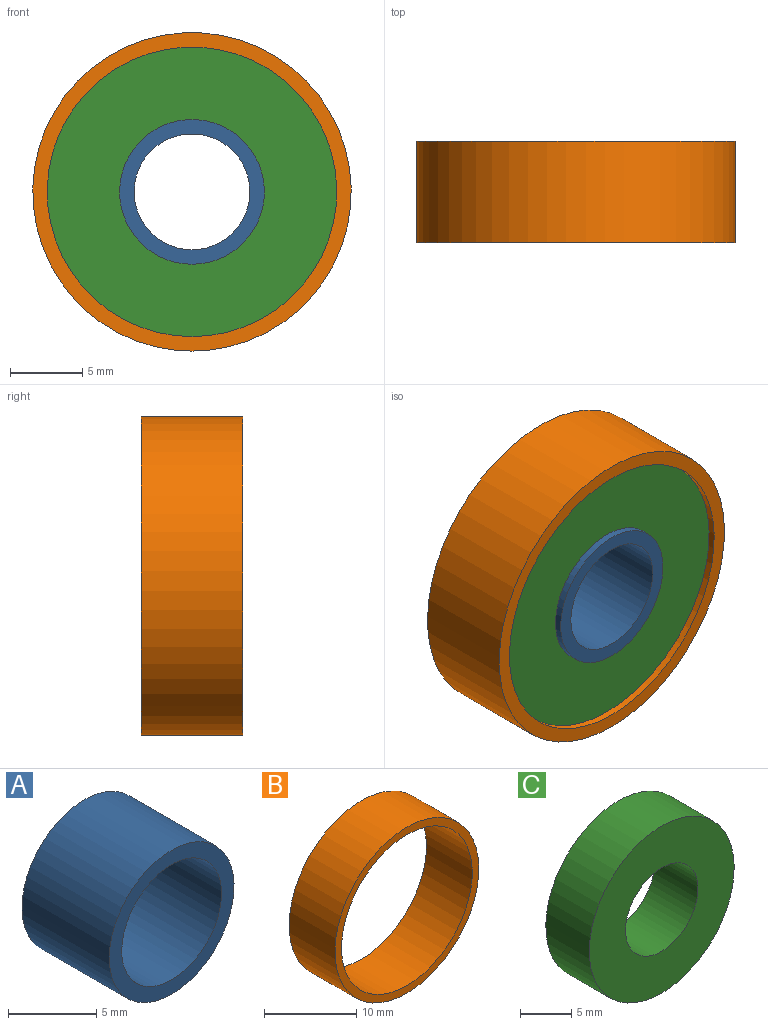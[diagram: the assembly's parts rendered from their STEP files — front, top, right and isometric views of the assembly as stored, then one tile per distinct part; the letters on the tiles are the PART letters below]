
ASSEMBLY  parts=3 mates=2
PART A: 4 faces, bbox 10x7x10 mm
  f0: cylinder r=4mm len=8mm, axis (0,1,0), area 175.9mm2, adj f2,f3
  f1: cylinder r=5mm len=10mm, axis (0,1,0), area 219.9mm2, adj f2,f3
  f2: plane 10x10mm, normal (0,-1,0), area 28.3mm2, adj f0,f1
  f3: plane 10x10mm, normal (0,1,0), area 28.3mm2, adj f0,f1
PART B: 4 faces, bbox 22x7x22 mm
  f0: cylinder r=10mm len=20mm, axis (0,1,0), area 439.8mm2, adj f2,f3
  f1: cylinder r=11mm len=22mm, axis (0,1,0), area 483.8mm2, adj f2,f3
  f2: plane 22x22mm, normal (0,-1,0), area 66mm2, adj f0,f1
  f3: plane 22x22mm, normal (0,1,0), area 66mm2, adj f0,f1
PART C: 4 faces, bbox 20x6x20 mm
  f0: cylinder r=5mm len=10mm, axis (0,1,0), area 188.5mm2, adj f2,f3
  f1: cylinder r=10mm len=20mm, axis (0,1,0), area 377mm2, adj f2,f3
  f2: plane 20x20mm, normal (0,-1,0), area 235.6mm2, adj f0,f1
  f3: plane 20x20mm, normal (0,1,0), area 235.6mm2, adj f0,f1
PLACE A t=(-3.61,-0.63,4.03)mm
PLACE B t=(-3.61,-0.63,4.03)mm
PLACE C t=(-3.61,-0.63,4.03)mm
MATE fastened C.f0 <-> B.f0  axis (0,1,0) through (-3.61,-0.63,4.03)mm
MATE fastened A.f0 <-> C.f0  axis (0,1,0) through (-3.61,-0.63,4.03)mm
